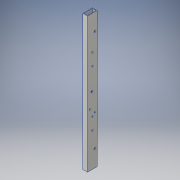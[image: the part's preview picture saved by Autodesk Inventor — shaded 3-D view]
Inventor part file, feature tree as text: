
AUTODESK INVENTOR PART (.ipt)
format: ipt  version: 2016 (Build 200138000, 138)  size: 165,376 bytes
history: native  units: in
note: dims shown in document units (in); Inventor stores cm internally (conversion verified against a paired STEP export)
features: extrude x3, sketch x2
ambient origin geometry x8: Origin, YZ Plane, XZ Plane, XY Plane, X Axis, Y Axis, Z Axis, Center Point
bodies: Solid1 (feature_tree)
feature tree (5):
  extrude  "Extrusion1"  Depth=2.0in
  sketch  "Sketch2"  dims[d2=0.125in d3=28.0in d4=0.0in d6=14.0in d7=1.125in d8=1.0in d9=0.0in d10=0.375in d11=1.5in d14=1.5in d16=10.5in d17=10.5in d18=0.2656in d19=1.0in d20=7.0in d22=9.5in d23=1.0in d25=1.0in d26=7.0in d28=1.0in d29=9.5in d30=0.2656in d31=0.2656in d32=0.5in d33=0.5in d34=1.0in d35=1.5in d36=1.0in d37=0.0in d38=2.5in]
  extrude  "Extrusion2"  Depth=28.0in TaperAngle=0.0deg
  extrude  "Extrusion3"  Depth=1.0in
  sketch  "Sketch1"  dims[d0=1.0in d1=2.0in]
